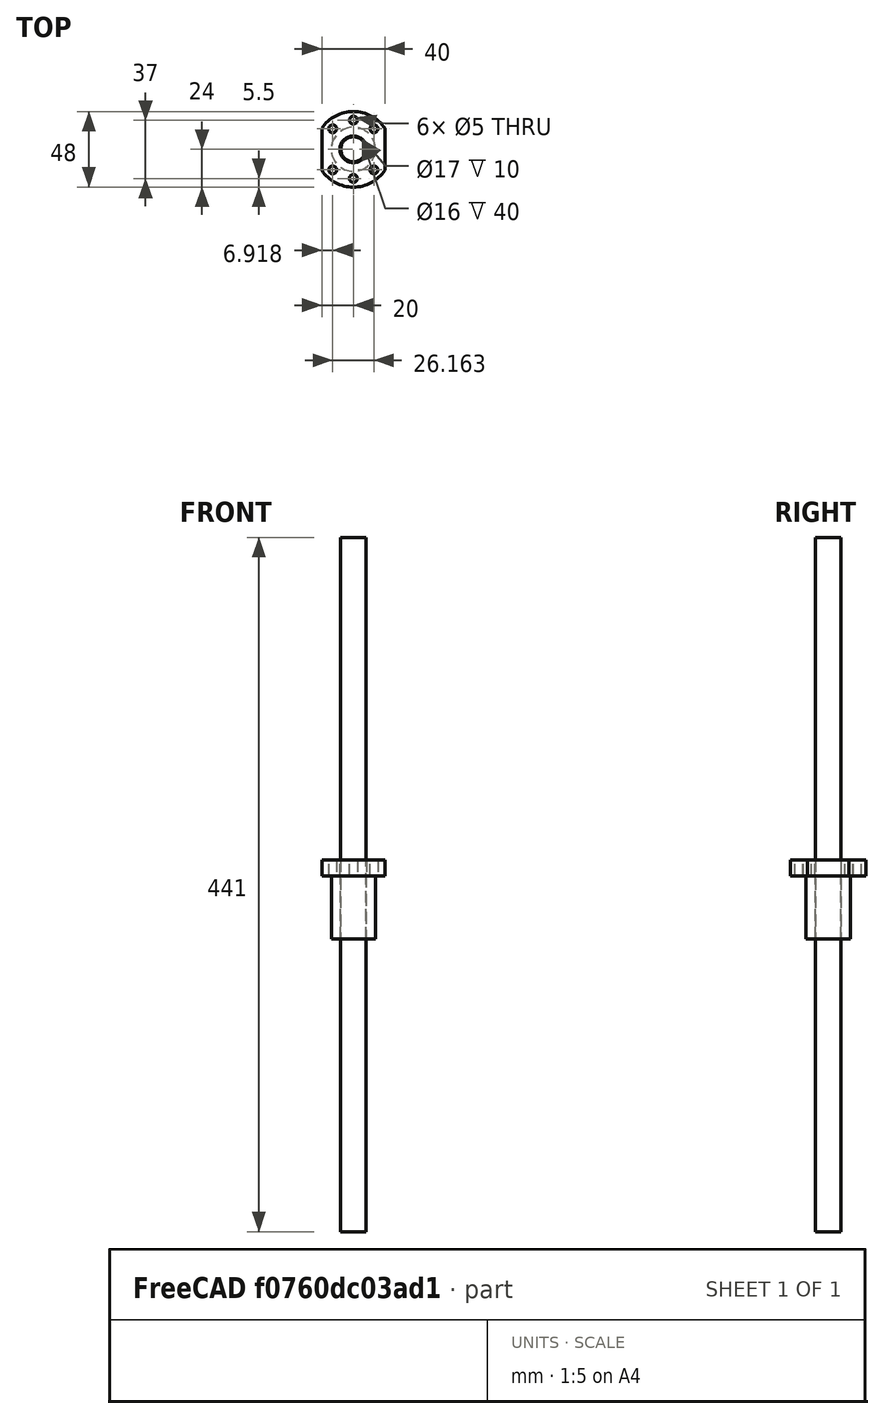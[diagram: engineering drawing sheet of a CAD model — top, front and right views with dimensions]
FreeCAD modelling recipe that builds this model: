
FCSTD DOCUMENT  (FreeCAD 0.14R3702 (Git))
Label: simple_ballscrew_500mm
License: CC-BY 3.0
LicenseURL: http://creativecommons.org/licenses/by/3.0/
objects: Sketcher::SketchObject×2, PartDesign::Pad×2, Part::Feature×1, Part::Torus×1, Part::FeaturePython×1, Part::Cut×1, Part::MultiFuse×1
note: 11 computed .brp shape members not serialized (recipe doc carries the construction recipe); baked Part::Feature solids carry a one-line shape summary decoded from their .brp

FEATURE [Sketcher::SketchObject] Sketch
  sketch-geometry (1):
    g0: Circle CenterX=0 CenterY=0 CenterZ=0 NormalX=0 NormalY=0 NormalZ=1 Radius=8
  constraints (2):
    c: Coincident(g0,g-1)
    c: Radius(g0) = 8
FEATURE [PartDesign::Pad] Pad001
  Length = 441
  Length2 = 1
  Sketch = -> Sketch
  Type = 0
FEATURE [Sketcher::SketchObject] Sketch001
  Placement = pos=(0,0,0) rot=(1,0,0;3.14159rad)
  Support = -> Pad001 [Face2]
  sketch-geometry (1):
    g0: Circle CenterX=0 CenterY=0 CenterZ=0 NormalX=0 NormalY=0 NormalZ=1 Radius=5
  constraints (2):
    c: Coincident(g0,g-1)
    c: Radius(g0) = 5
FEATURE [PartDesign::Pad] Pad002  label="Pad004"
  Length = 11
  Length2 = 492
  Sketch = -> Sketch001
  Type = 4
FEATURE [Part::Feature] Pad003  label="Pad002"
  Placement = pos=(6.987e-09,-1.70514e-05,236) rot=(1,0,0;3.14159rad)
  shape: bbox 40 x 48 x 50 mm, 17 faces (baked)
FEATURE [Part::Torus] Torus
  Angle1 = -180
  Angle2 = 180
  Angle3 = 360
  Placement = pos=(0,0,2) rot=(0,0,1;0rad)
  Radius1 = 8
  Radius2 = 2
FEATURE [Part::FeaturePython] Array  # Draft array (typed FeaturePython)
  Angle = 360
  ArrayType = 0
  Axis = (0,0,1)
  Base = -> Torus
  Center = (0,0,0)
  IntervalX = (1,0,0)
  IntervalY = (0,1,0)
  IntervalZ = (0,0,5)
  NumberPolar = 1
  NumberX = 1
  NumberY = 1
  NumberZ = 88
FEATURE [Part::Cut] Cut
  Base = -> Pad002
  Tool = -> Array
FEATURE [Part::MultiFuse] Fusion
  Shapes = -> [Pad003,Cut]
